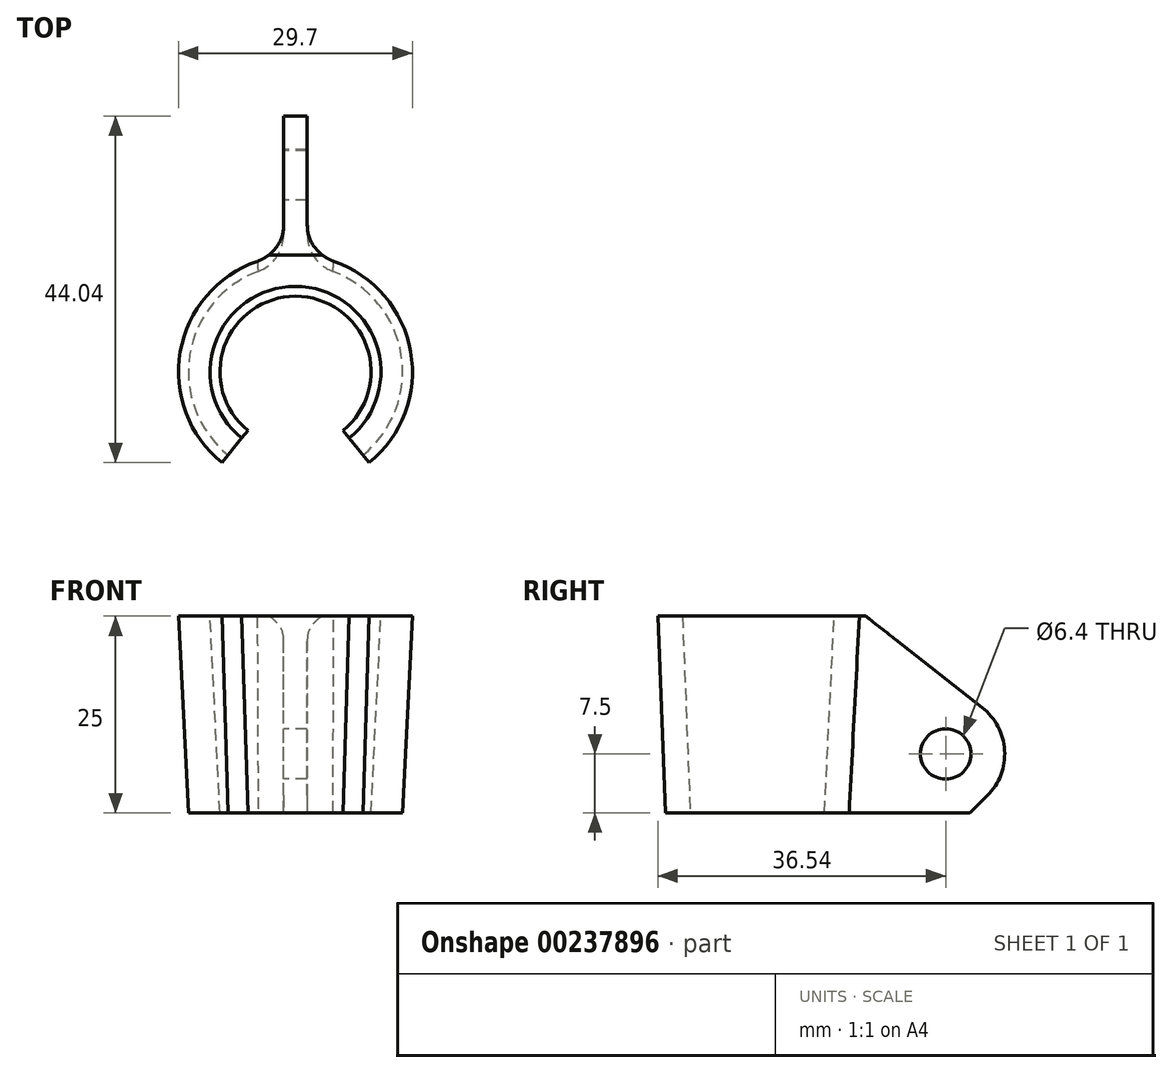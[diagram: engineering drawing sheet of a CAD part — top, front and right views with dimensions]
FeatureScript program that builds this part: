
annotation { "Feature Type Name" : "Feature", "Feature Type Description" : "" }
export const myFeature = defineFeature(function(context is Context, id is Id, definition is map)
    precondition{}
    {
        {
            var Q0;
            Q0=qCreatedBy(makeId("Right.planeOp"),FACE);
            var sketch = newSketch(context, id + "F0", { "sketchPlane" : qUnion([Q0])});
            skLineSegment(sketch, "E0", {"start": v(13.6, 0) * mm, "end": v(14.85, 25) * mm});
            skLineSegment(sketch, "E1", {"start": v(14.85, 25) * mm, "end": v(10.85, 25) * mm});
            skLineSegment(sketch, "E2", {"start": v(10.85, 25) * mm, "end": v(9.6, 0) * mm});
            skLineSegment(sketch, "E3", {"start": v(9.6, 0) * mm, "end": v(13.6, 0) * mm});
            skLineSegment(sketch, "E4", {"start": v(0, 0) * mm, "end": v(0, 25) * mm, "construction": true});
            skSolve(sketch);
        }
        {
            var Q0;
            Q0=makeQuery(id+"F0.imprint","IMPRINT",FACE,{"disambiguationData":[TD([[makeQuery(id+"F0.imprint","IMPRINT",EDGE,{"derivedFrom":sQuery(id+"F0.wireOp",EDGE,"E0")}),1.0]])]});
            var Q1;
            Q1=sQuery(id+"F0.wireOp",EDGE,"E4");
            revolve(context, id + "F1", {"surfaceOperationType" : NewSurfaceOperationType.NEW, "entities" : qUnion([Q0]), "axis" : qUnion([Q1]), "revolveType" : RevolveType.SYMMETRIC, "angle" : 282 * degree});
        }
        {
            var Q0;
            Q0=qCreatedBy(makeId("Right.planeOp"),FACE);
            var sketch = newSketch(context, id + "F2", { "sketchPlane" : qUnion([Q0])});
            skLineSegment(sketch, "E5", {"start": v(10.85, 25) * mm, "end": v(14.85, 25) * mm});
            skLineSegment(sketch, "E6", {"start": v(29.63, 13.4) * mm, "end": v(14.85, 25) * mm});
            skLineSegment(sketch, "E7", {"start": v(25, 0) * mm, "end": v(9.6, 0) * mm});
            skLineSegment(sketch, "E8", {"start": v(10.85, 25) * mm, "end": v(9.6, 0) * mm});
            skArc(sketch, "E9", {"start": v(30.3, 2.2) * mm, "mid": v(32.49, 7.95) * mm, "end": v(29.63, 13.4) * mm});
            skCircle(sketch, "E10", {"center": v(25, 7.5) * mm, "radius": 3.2 * mm});
            skLineSegment(sketch, "E11", {"start": v(30.3, 2.2) * mm, "end": v(28.1, 0) * mm});
            skLineSegment(sketch, "E12", {"start": v(28.1, 0) * mm, "end": v(25, 0) * mm});
            skSolve(sketch);
        }
        {
            var Q0;
            Q0=makeQuery(id+"F2.imprint","IMPRINT",FACE,{"disambiguationData":[TD([[makeQuery(id+"F2.imprint","IMPRINT",EDGE,{"derivedFrom":sQuery(id+"F2.wireOp",EDGE,"E5")}),-1.0]])]});
            extrude(context, id + "F3", {"entities" : qUnion([Q0]), "operationType" : NewBodyOperationType.ADD, "depth" : 3 * mm, "symmetric" : true});
        }
        {
            var Q0;
            Q0=makeQuery(id+"F3.boolean.opBoolean","INTERSECT",EDGE,{"derivedFrom":[makeQuery(id+"F1.opRevolve","SWEPT_FACE",FACE,{"disambiguationData":[OSD([sQuery(id+"F0.wireOp",EDGE,"E0")])]}),makeQuery(id+"F3.opExtrude","CAP_FACE",FACE,{"disambiguationData":[OSD([sQuery(id+"F2.wireOp",EDGE,"E5"),sQuery(id+"F2.wireOp",EDGE,"E6"),sQuery(id+"F2.wireOp",EDGE,"E7"),sQuery(id+"F2.wireOp",EDGE,"E8"),sQuery(id+"F2.wireOp",EDGE,"E9"),sQuery(id+"F2.wireOp",EDGE,"E10")])],"isStart":false})]});
            var Q1;
            Q1=makeQuery(id+"F3.boolean.opBoolean","INTERSECT",EDGE,{"derivedFrom":[makeQuery(id+"F1.opRevolve","SWEPT_FACE",FACE,{"disambiguationData":[OSD([sQuery(id+"F0.wireOp",EDGE,"E0")])]}),makeQuery(id+"F3.opExtrude","CAP_FACE",FACE,{"disambiguationData":[OSD([sQuery(id+"F2.wireOp",EDGE,"E5"),sQuery(id+"F2.wireOp",EDGE,"E6"),sQuery(id+"F2.wireOp",EDGE,"E7"),sQuery(id+"F2.wireOp",EDGE,"E8"),sQuery(id+"F2.wireOp",EDGE,"E9"),sQuery(id+"F2.wireOp",EDGE,"E10")])],"isStart":true})]});
            fillet(context, id + "F4", {"entities" : qUnion([Q0, Q1]), "radius" : 5 * mm, "tangentPropagation" : true, "defaultsChanged" : true, "vertexSettings" : [], "allowEdgeOverflow" : false});
        }
    });
